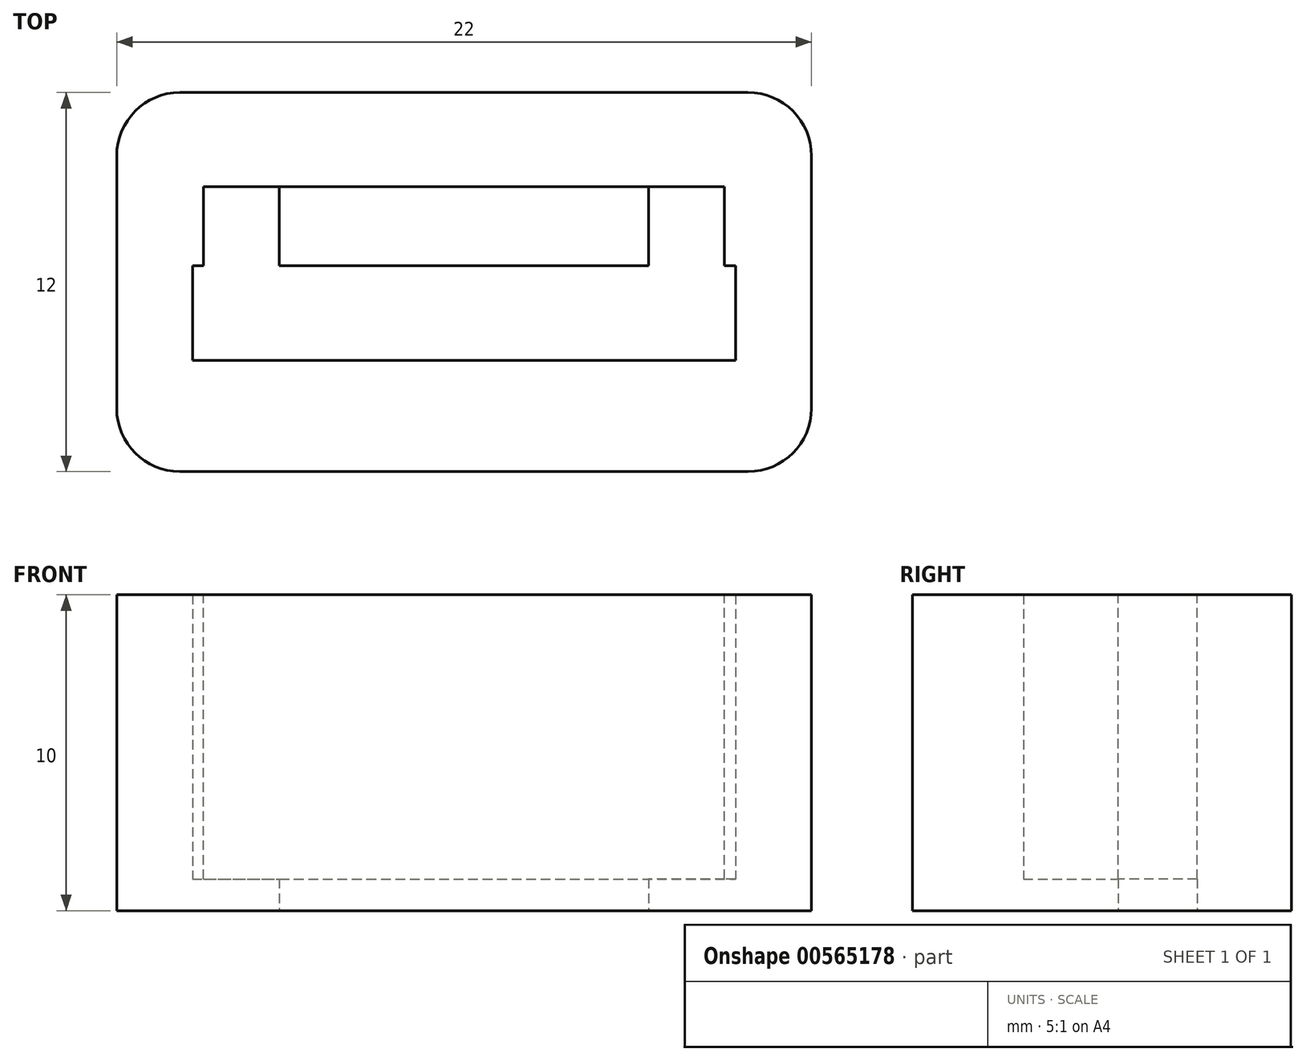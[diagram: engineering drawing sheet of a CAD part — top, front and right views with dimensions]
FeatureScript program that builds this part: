
annotation { "Feature Type Name" : "Feature", "Feature Type Description" : "" }
export const myFeature = defineFeature(function(context is Context, id is Id, definition is map)
    precondition{}
    {
        {
            var Q0;
            Q0=qCreatedBy(makeId("Top.planeOp"),FACE);
            var sketch = newSketch(context, id + "F0", { "sketchPlane" : qUnion([Q0])});
            skLineSegment(sketch, "E0.bottom", {"start": v(11, 6) * mm, "end": v(-11, 6) * mm});
            skLineSegment(sketch, "E0.top", {"start": v(11, -6) * mm, "end": v(-11, -6) * mm});
            skLineSegment(sketch, "E0.left", {"start": v(11, 6) * mm, "end": v(11, -6) * mm});
            skLineSegment(sketch, "E0.right", {"start": v(-11, 6) * mm, "end": v(-11, -6) * mm});
            skPoint(sketch, "E0.middle", {"position": v(0, 0) * mm});
            skLineSegment(sketch, "E1", {"start": v(0, 0) * mm, "end": v(0, -5.42) * mm, "construction": true});
            skLineSegment(sketch, "E2", {"start": v(0, -5.42) * mm, "end": v(0, 5.9) * mm, "construction": true});
            skLineSegment(sketch, "E3", {"start": v(0, 3.02) * mm, "end": v(5.85, 3.02) * mm});
            skLineSegment(sketch, "E4", {"start": v(5.85, 3.02) * mm, "end": v(5.85, 0.52) * mm});
            skLineSegment(sketch, "E5", {"start": v(5.85, 0.52) * mm, "end": v(8.6, 0.52) * mm});
            skLineSegment(sketch, "E6", {"start": v(8.6, 0.52) * mm, "end": v(8.6, -2.48) * mm});
            skLineSegment(sketch, "E7", {"start": v(8.6, -2.48) * mm, "end": v(0, -2.48) * mm});
            skLineSegment(sketch, "E8.MirrorCS", {"start": v(0, 3.02) * mm, "end": v(-5.85, 3.02) * mm});
            skLineSegment(sketch, "E9.MirrorCS", {"start": v(-5.85, 3.02) * mm, "end": v(-5.85, 0.52) * mm});
            skLineSegment(sketch, "E10.MirrorCS", {"start": v(-5.85, 0.52) * mm, "end": v(-8.6, 0.52) * mm});
            skLineSegment(sketch, "E11.MirrorCS", {"start": v(-8.6, 0.52) * mm, "end": v(-8.6, -2.48) * mm});
            skLineSegment(sketch, "E12.MirrorCS", {"start": v(-8.6, -2.48) * mm, "end": v(0, -2.48) * mm});
            skLineSegment(sketch, "E13", {"start": v(-5.85, 0.52) * mm, "end": v(5.85, 0.52) * mm});
            skSolve(sketch);
        }
        {
            var Q0;
            Q0=makeQuery(id+"F0.imprint","IMPRINT",FACE,{"disambiguationData":[TD([[makeQuery(id+"F0.imprint","IMPRINT",EDGE,{"derivedFrom":sQuery(id+"F0.wireOp",EDGE,"E0.bottom")}),1.0]])]});
            var Q1;
            Q1=makeQuery(id+"F0.imprint","IMPRINT",FACE,{"disambiguationData":[TD([[makeQuery(id+"F0.imprint","IMPRINT",EDGE,{"derivedFrom":sQuery(id+"F0.wireOp",EDGE,"E5")}),-1.0]])]});
            extrude(context, id + "F1", {"entities" : qUnion([Q0, Q1]), "depth" : 1 * mm, "offsetDistance" : 25 * mm});
        }
        {
            var Q0;
            Q0 = qSketchRegion(id + "F0", true);
            extrude(context, id + "F2", {"entities" : qUnion([Q0]), "operationType" : NewBodyOperationType.ADD, "depth" : 10 * mm, "offsetDistance" : 25 * mm});
        }
        {
            var Q0;
            Q0=makeQuery(id+"F2.opExtrude","CAP_FACE",FACE,{"disambiguationData":[OSD([sQuery(id+"F0.wireOp",EDGE,"E0.bottom"),sQuery(id+"F0.wireOp",EDGE,"E0.top"),sQuery(id+"F0.wireOp",EDGE,"E0.left"),sQuery(id+"F0.wireOp",EDGE,"E0.right"),sQuery(id+"F0.wireOp",EDGE,"E3"),sQuery(id+"F0.wireOp",EDGE,"E4"),sQuery(id+"F0.wireOp",EDGE,"E5"),sQuery(id+"F0.wireOp",EDGE,"E6"),sQuery(id+"F0.wireOp",EDGE,"E7"),sQuery(id+"F0.wireOp",EDGE,"E8.MirrorCS"),sQuery(id+"F0.wireOp",EDGE,"E9.MirrorCS"),sQuery(id+"F0.wireOp",EDGE,"E10.MirrorCS"),sQuery(id+"F0.wireOp",EDGE,"E11.MirrorCS"),sQuery(id+"F0.wireOp",EDGE,"E12.MirrorCS")])],"isStart":false});
            var sketch = newSketch(context, id + "F3", { "sketchPlane" : qUnion([Q0])});
            skLineSegment(sketch, "E14.bottom", {"start": v(-5.85, 0.52) * mm, "end": v(-8.25, 0.52) * mm});
            skLineSegment(sketch, "E14.top", {"start": v(-5.85, 3.02) * mm, "end": v(-8.25, 3.02) * mm});
            skLineSegment(sketch, "E14.left", {"start": v(-5.85, 0.52) * mm, "end": v(-5.85, 3.02) * mm});
            skLineSegment(sketch, "E14.right", {"start": v(-8.25, 0.52) * mm, "end": v(-8.25, 3.02) * mm});
            skLineSegment(sketch, "E15.bottom", {"start": v(5.85, 0.52) * mm, "end": v(8.25, 0.52) * mm});
            skLineSegment(sketch, "E15.top", {"start": v(5.85, 3.02) * mm, "end": v(8.25, 3.02) * mm});
            skLineSegment(sketch, "E15.left", {"start": v(5.85, 0.52) * mm, "end": v(5.85, 3.02) * mm});
            skLineSegment(sketch, "E15.right", {"start": v(8.25, 0.52) * mm, "end": v(8.25, 3.02) * mm});
            skSolve(sketch);
        }
        {
            var Q0;
            Q0=makeQuery(id+"F3.imprint","IMPRINT",FACE,{"disambiguationData":[TD([[makeQuery(id+"F3.imprint","IMPRINT",EDGE,{"derivedFrom":sQuery(id+"F3.wireOp",EDGE,"E14.bottom")}),-1.0]])]});
            var Q1;
            Q1=makeQuery(id+"F3.imprint","IMPRINT",FACE,{"disambiguationData":[TD([[makeQuery(id+"F3.imprint","IMPRINT",EDGE,{"derivedFrom":sQuery(id+"F3.wireOp",EDGE,"E15.bottom")}),1.0]])]});
            var Q2;
            Q2=makeQuery(id+"F1.opExtrude","CAP_FACE",FACE,{"disambiguationData":[OSD([sQuery(id+"F0.wireOp",EDGE,"E0.bottom"),sQuery(id+"F0.wireOp",EDGE,"E0.top"),sQuery(id+"F0.wireOp",EDGE,"E0.left"),sQuery(id+"F0.wireOp",EDGE,"E0.right"),sQuery(id+"F0.wireOp",EDGE,"E3"),sQuery(id+"F0.wireOp",EDGE,"E4"),sQuery(id+"F0.wireOp",EDGE,"E8.MirrorCS"),sQuery(id+"F0.wireOp",EDGE,"E9.MirrorCS"),sQuery(id+"F0.wireOp",EDGE,"E13")])],"isStart":false});
            extrude(context, id + "F4", {"entities" : qUnion([Q0, Q1]), "operationType" : NewBodyOperationType.REMOVE, "endBound" : BoundingType.UP_TO_SURFACE, "oppositeDirection" : true, "depth" : 25 * mm, "endBoundEntityFace" : qUnion([Q2]), "offsetDistance" : 25 * mm});
        }
        {
            var Q0;
            {var subQ0=sQuery(id+"F0.wireOp",EDGE,"E0.right");var subQ1=sQuery(id+"F0.wireOp",EDGE,"E0.top");Q0=makeQuery(id+"F2.boolean.opBoolean","MERGE",EDGE,{"derivedFrom":[makeQuery(id+"F1.opExtrude","SWEPT_EDGE",EDGE,{"disambiguationData":[OSD([subQ1,subQ0])]}),makeQuery(id+"F2.opExtrude","SWEPT_EDGE",EDGE,{"disambiguationData":[OSD([subQ1,subQ0])]})]});}
            var Q1;
            {var subQ0=sQuery(id+"F0.wireOp",EDGE,"E0.left");var subQ1=sQuery(id+"F0.wireOp",EDGE,"E0.top");Q1=makeQuery(id+"F2.boolean.opBoolean","MERGE",EDGE,{"derivedFrom":[makeQuery(id+"F1.opExtrude","SWEPT_EDGE",EDGE,{"disambiguationData":[OSD([subQ1,subQ0])]}),makeQuery(id+"F2.opExtrude","SWEPT_EDGE",EDGE,{"disambiguationData":[OSD([subQ1,subQ0])]})]});}
            var Q2;
            {var subQ0=sQuery(id+"F0.wireOp",EDGE,"E0.right");var subQ1=sQuery(id+"F0.wireOp",EDGE,"E0.bottom");Q2=makeQuery(id+"F2.boolean.opBoolean","MERGE",EDGE,{"derivedFrom":[makeQuery(id+"F1.opExtrude","SWEPT_EDGE",EDGE,{"disambiguationData":[OSD([subQ1,subQ0])]}),makeQuery(id+"F2.opExtrude","SWEPT_EDGE",EDGE,{"disambiguationData":[OSD([subQ1,subQ0])]})]});}
            var Q3;
            {var subQ0=sQuery(id+"F0.wireOp",EDGE,"E0.left");var subQ1=sQuery(id+"F0.wireOp",EDGE,"E0.bottom");Q3=makeQuery(id+"F2.boolean.opBoolean","MERGE",EDGE,{"derivedFrom":[makeQuery(id+"F1.opExtrude","SWEPT_EDGE",EDGE,{"disambiguationData":[OSD([subQ1,subQ0])]}),makeQuery(id+"F2.opExtrude","SWEPT_EDGE",EDGE,{"disambiguationData":[OSD([subQ1,subQ0])]})]});}
            fillet(context, id + "F5", {"entities" : qUnion([Q0, Q1, Q2, Q3]), "radius" : 2 * mm, "tangentPropagation" : true, "allowEdgeOverflow" : false});
        }
    });
